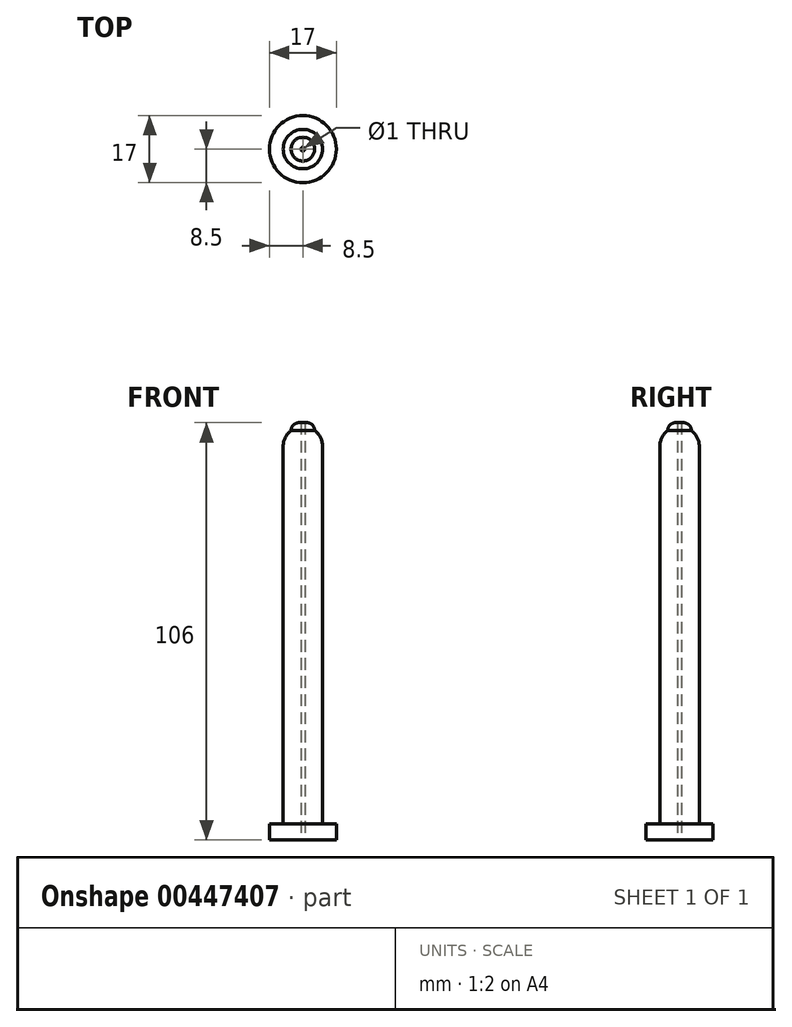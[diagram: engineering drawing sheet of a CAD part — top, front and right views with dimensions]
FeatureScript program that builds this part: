
annotation { "Feature Type Name" : "Feature", "Feature Type Description" : "" }
export const myFeature = defineFeature(function(context is Context, id is Id, definition is map)
    precondition{}
    {
        {
            var Q0;
            Q0=qCreatedBy(makeId("Top.planeOp"),FACE);
            var sketch = newSketch(context, id + "F0", { "sketchPlane" : qUnion([Q0])});
            skCircle(sketch, "E0", {"center": v(0, 0) * mm, "radius": 8.5 * mm});
            skSolve(sketch);
        }
        {
            var Q0;
            Q0=qSketchRegion(id+"F0",true);
            extrude(context, id + "F1", {"entities" : qUnion([Q0]), "depth" : 4 * mm});
        }
        {
            var Q0;
            Q0=qCreatedBy(makeId("Top.planeOp"),FACE);
            var sketch = newSketch(context, id + "F2", { "sketchPlane" : qUnion([Q0])});
            skCircle(sketch, "E1", {"center": v(0, 0) * mm, "radius": 5 * mm});
            skSolve(sketch);
        }
        {
            var Q0;
            Q0=qSketchRegion(id+"F2",true);
            extrude(context, id + "F3", {"entities" : qUnion([Q0]), "operationType" : NewBodyOperationType.ADD, "depth" : 100 * mm});
        }
        {
            var Q0;
            Q0=qCreatedBy(makeId("Right.planeOp"),FACE);
            var sketch = newSketch(context, id + "F4", { "sketchPlane" : qUnion([Q0])});
            skLineSegment(sketch, "E2", {"start": v(0, 100) * mm, "end": v(5, 100) * mm});
            skArc(sketch, "E3", {"start": v(5, 100) * mm, "mid": v(3.54, 103.54) * mm, "end": v(0, 105) * mm});
            skLineSegment(sketch, "E4", {"start": v(0, 106) * mm, "end": v(1, 106) * mm});
            skLineSegment(sketch, "E5", {"start": v(3, 104) * mm, "end": v(0, 104) * mm});
            skLineSegment(sketch, "E6", {"start": v(0, 106) * mm, "end": v(0, 100) * mm});
            skArc(sketch, "E7", {"start": v(3, 104) * mm, "mid": v(2.41, 105.41) * mm, "end": v(1, 106) * mm});
            skSolve(sketch);
        }
        {
            var Q0;
            {var subQ0=sQuery(id+"F4.wireOp",EDGE,"E2");Q0=makeQuery(id+"F4.imprint","IMPRINT",FACE,{"disambiguationData":[TD([[makeQuery(id+"F4.imprint","IMPRINT",EDGE,{"derivedFrom":subQ0}),1.0]])]});}
            var Q1;
            {var subQ4=sQuery(id+"F4.wireOp",EDGE,"E4");Q1=makeQuery(id+"F4.imprint","IMPRINT",FACE,{"disambiguationData":[TD([[makeQuery(id+"F4.imprint","IMPRINT",EDGE,{"derivedFrom":subQ4}),-1.0]])]});}
            var Q2;
            {var subQ3=sQuery(id+"F4.wireOp",EDGE,"E5");Q2=makeQuery(id+"F4.imprint","IMPRINT",FACE,{"disambiguationData":[TD([[makeQuery(id+"F4.imprint","IMPRINT",EDGE,{"derivedFrom":subQ3}),-1.0]])]});}
            var Q3;
            Q3=sQuery(id+"F4.wireOp",EDGE,"E6");
            revolve(context, id + "F5", {"operationType" : NewBodyOperationType.ADD, "entities" : qUnion([Q0, Q1, Q2]), "axis" : qUnion([Q3]), "revolveType" : RevolveType.FULL});
        }
        {
            var Q0;
            Q0=makeQuery(id+"F1.opExtrude","CAP_FACE",FACE,{"disambiguationData":[OSD([sQuery(id+"F0.wireOp",EDGE,"E0")])],"isStart":true});
            var sketch = newSketch(context, id + "F6", { "sketchPlane" : qUnion([Q0])});
            skCircle(sketch, "E8", {"center": v(0, 0) * mm, "radius": 0.5 * mm});
            skSolve(sketch);
        }
        {
            var Q0;
            Q0 = qSketchRegion(id + "F6", true);
            extrude(context, id + "F7", {"entities" : qUnion([Q0]), "operationType" : NewBodyOperationType.REMOVE, "oppositeDirection" : true, "depth" : 169.1 * mm});
        }
    });
